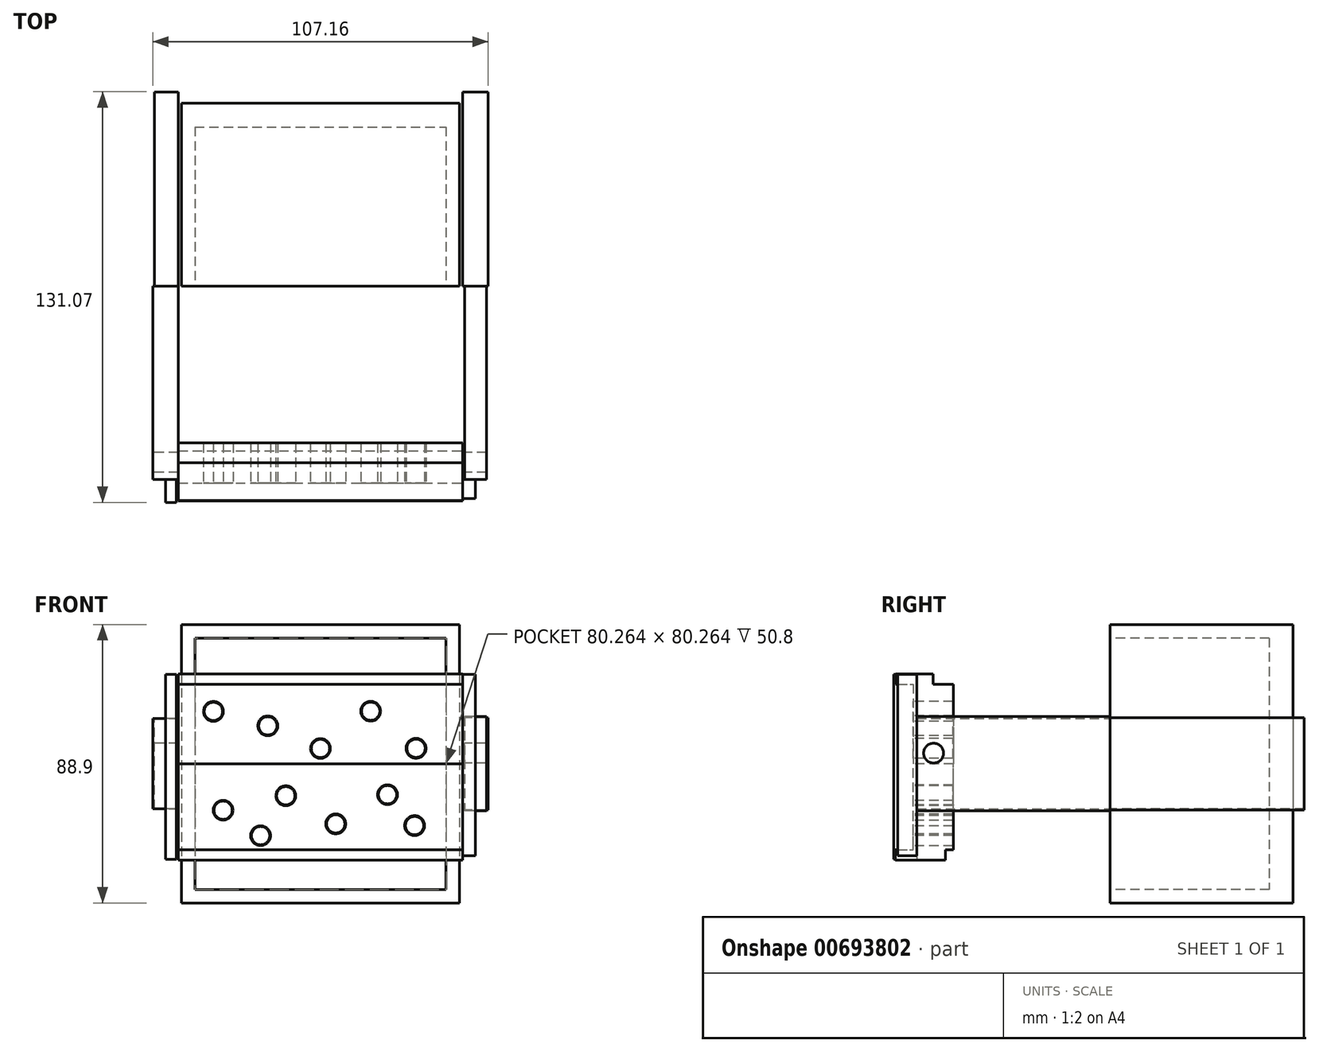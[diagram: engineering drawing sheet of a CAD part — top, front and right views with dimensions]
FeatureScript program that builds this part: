
annotation { "Feature Type Name" : "Feature", "Feature Type Description" : "" }
export const myFeature = defineFeature(function(context is Context, id is Id, definition is map)
    precondition{}
    {
        {
            var Q0;
            Q0=qCreatedBy(makeId("Front.planeOp"),FACE);
            var sketch = newSketch(context, id + "F0", { "sketchPlane" : qUnion([Q0])});
            skLineSegment(sketch, "E0.bottom", {"start": v(-44.45, 44.45) * mm, "end": v(44.45, 44.45) * mm});
            skLineSegment(sketch, "E0.top", {"start": v(-44.45, -44.45) * mm, "end": v(44.45, -44.45) * mm});
            skLineSegment(sketch, "E0.left", {"start": v(-44.45, 44.45) * mm, "end": v(-44.45, -44.45) * mm});
            skLineSegment(sketch, "E0.right", {"start": v(44.45, 44.45) * mm, "end": v(44.45, -44.45) * mm});
            skPoint(sketch, "E0.middle", {"position": v(0, 0) * mm});
            skSolve(sketch);
        }
        {
            var Q0;
            Q0 = qSketchRegion(id + "F0", true);
            extrude(context, id + "F1", {"entities" : qUnion([Q0]), "oppositeDirection" : true, "depth" : 58.42 * mm, "offsetDistance" : 25.4 * mm});
        }
        {
            var Q0;
            Q0=makeQuery(id+"F1.opExtrude","CAP_FACE",FACE,{"disambiguationData":[OSD([sQuery(id+"F0.wireOp",EDGE,"E0.bottom"),sQuery(id+"F0.wireOp",EDGE,"E0.top"),sQuery(id+"F0.wireOp",EDGE,"E0.left"),sQuery(id+"F0.wireOp",EDGE,"E0.right")])],"isStart":true});
            var sketch = newSketch(context, id + "F2", { "sketchPlane" : qUnion([Q0])});
            skLineSegment(sketch, "E1.0", {"start": v(-40.13, 40.13) * mm, "end": v(40.13, 40.13) * mm});
            skLineSegment(sketch, "E1.1", {"start": v(-40.13, 40.13) * mm, "end": v(-40.13, -40.13) * mm});
            skLineSegment(sketch, "E1.2", {"start": v(-40.13, -40.13) * mm, "end": v(40.13, -40.13) * mm});
            skLineSegment(sketch, "E1.3", {"start": v(40.13, 40.13) * mm, "end": v(40.13, -40.13) * mm});
            skSolve(sketch);
        }
        {
            var Q0;
            Q0=makeQuery(id+"F2.imprint","IMPRINT",FACE,{"disambiguationData":[TD([[makeQuery(id+"F2.imprint","IMPRINT",EDGE,{"derivedFrom":sQuery(id+"F2.wireOp",EDGE,"E1.0")}),-1.0]])]});
            extrude(context, id + "F3", {"entities" : qUnion([Q0]), "operationType" : NewBodyOperationType.REMOVE, "oppositeDirection" : true, "depth" : 50.8 * mm, "offsetDistance" : 25.4 * mm});
        }
        {
            var Q0;
            Q0=qCreatedBy(makeId("Front.planeOp"),FACE);
            var sketch = newSketch(context, id + "F4", { "sketchPlane" : qUnion([Q0])});
            skLineSegment(sketch, "E2.bottom", {"start": v(-53, -14.45) * mm, "end": v(-45.4, -14.45) * mm});
            skLineSegment(sketch, "E2.top", {"start": v(-53, 14.45) * mm, "end": v(-45.4, 14.45) * mm});
            skLineSegment(sketch, "E2.left", {"start": v(-53, -14.45) * mm, "end": v(-53, 14.45) * mm});
            skLineSegment(sketch, "E2.right", {"start": v(-45.4, -14.45) * mm, "end": v(-45.4, 14.45) * mm});
            skPoint(sketch, "E2.middle", {"position": v(-49.2, 0) * mm});
            skLineSegment(sketch, "E3.bottom", {"start": v(53.58, 14.75) * mm, "end": v(45.4, 14.75) * mm});
            skLineSegment(sketch, "E3.top", {"start": v(53.58, -14.75) * mm, "end": v(45.4, -14.75) * mm});
            skLineSegment(sketch, "E3.left", {"start": v(53.58, 14.75) * mm, "end": v(53.58, -14.75) * mm});
            skLineSegment(sketch, "E3.right", {"start": v(45.4, 14.75) * mm, "end": v(45.4, -14.75) * mm});
            skPoint(sketch, "E3.middle", {"position": v(49.5, 0) * mm});
            skSolve(sketch);
        }
        {
            var Q0;
            Q0 = qSketchRegion(id + "F4", true);
            extrude(context, id + "F5", {"entities" : qUnion([Q0]), "oppositeDirection" : true, "depth" : 61.98 * mm, "offsetDistance" : 25.4 * mm});
        }
        {
            var Q0;
            Q0=qCreatedBy(makeId("Front.planeOp"),FACE);
            var sketch = newSketch(context, id + "F6", { "sketchPlane" : qUnion([Q0])});
            skLineSegment(sketch, "E4.bottom", {"start": v(-45.4, 14.45) * mm, "end": v(-53.58, 14.45) * mm});
            skLineSegment(sketch, "E4.top", {"start": v(-45.4, -14.45) * mm, "end": v(-53.58, -14.45) * mm});
            skLineSegment(sketch, "E4.left", {"start": v(-45.4, 14.45) * mm, "end": v(-45.4, -14.45) * mm});
            skLineSegment(sketch, "E4.right", {"start": v(-53.58, 14.45) * mm, "end": v(-53.58, -14.45) * mm});
            skPoint(sketch, "E4.middle", {"position": v(-49.5, 0) * mm});
            skLineSegment(sketch, "E5.bottom", {"start": v(53, 15.04) * mm, "end": v(46, 15.04) * mm});
            skLineSegment(sketch, "E5.top", {"start": v(53, -15.04) * mm, "end": v(46, -15.04) * mm});
            skLineSegment(sketch, "E5.left", {"start": v(53, 15.04) * mm, "end": v(53, -15.04) * mm});
            skLineSegment(sketch, "E5.right", {"start": v(46, 15.04) * mm, "end": v(46, -15.04) * mm});
            skPoint(sketch, "E5.middle", {"position": v(49.5, 0) * mm});
            skSolve(sketch);
        }
        {
            var Q0;
            Q0 = qSketchRegion(id + "F6", true);
            extrude(context, id + "F7", {"entities" : qUnion([Q0]), "depth" : 61.72 * mm, "offsetDistance" : 25.4 * mm});
        }
        {
            var Q0;
            Q0=qCreatedBy(makeId("Front.planeOp"),FACE);
            var sketch = newSketch(context, id + "F8", { "sketchPlane" : qUnion([Q0])});
            skLineSegment(sketch, "E6.bottom", {"start": v(-52.7, -14.16) * mm, "end": v(52.7, -14.16) * mm});
            skLineSegment(sketch, "E6.top", {"start": v(-52.7, 14.16) * mm, "end": v(52.7, 14.16) * mm});
            skLineSegment(sketch, "E6.left", {"start": v(-52.7, -14.16) * mm, "end": v(-52.7, 14.16) * mm});
            skLineSegment(sketch, "E6.right", {"start": v(52.7, -14.16) * mm, "end": v(52.7, 14.16) * mm});
            skPoint(sketch, "E6.middle", {"position": v(0, 0) * mm});
            skSolve(sketch);
        }
        {
            var Q0;
            Q0=makeQuery(id+"F8.imprint","IMPRINT",FACE,{"disambiguationData":[TD([[makeQuery(id+"F8.imprint","IMPRINT",EDGE,{"derivedFrom":sQuery(id+"F8.wireOp",EDGE,"E6.bottom")}),1.0]])]});
            extrude(context, id + "F9", {"entities" : qUnion([Q0]), "depth" : 39.12 * mm, "offsetDistance" : 25.4 * mm});
        }
        {
            var Q0;
            Q0=makeQuery(id+"F7.opExtrude","SWEPT_FACE",FACE,{"disambiguationData":[OSD([sQuery(id+"F6.wireOp",EDGE,"E4.right")])]});
            var sketch = newSketch(context, id + "F10", { "sketchPlane" : qUnion([Q0])});
            skLineSegment(sketch, "E7.bottom", {"start": v(51.15, -3.82) * mm, "end": v(61.6, -3.82) * mm});
            skLineSegment(sketch, "E7.top", {"start": v(51.15, 10.58) * mm, "end": v(61.6, 10.58) * mm});
            skLineSegment(sketch, "E7.left", {"start": v(51.15, -3.82) * mm, "end": v(51.15, 10.58) * mm});
            skLineSegment(sketch, "E7.right", {"start": v(61.6, -3.82) * mm, "end": v(61.6, 10.58) * mm});
            skPoint(sketch, "E7.middle", {"position": v(56.38, 3.38) * mm});
            skSolve(sketch);
        }
        {
            var Q0;
            Q0=sQuery(id+"F10.wireOp",VERTEX,"E7.middle");
            var Q1;
            Q1=makeQuery(id+"F7.opExtrude","SWEPT_BODY",BODY,{"disambiguationData":[OSD([sQuery(id+"F6.wireOp",EDGE,"E4.bottom"),sQuery(id+"F6.wireOp",EDGE,"E4.top"),sQuery(id+"F6.wireOp",EDGE,"E4.left"),sQuery(id+"F6.wireOp",EDGE,"E4.right")])]});
            var Q2;
            Q2=makeQuery(id+"F7.opExtrude","SWEPT_BODY",BODY,{"disambiguationData":[OSD([sQuery(id+"F6.wireOp",EDGE,"E5.bottom"),sQuery(id+"F6.wireOp",EDGE,"E5.top"),sQuery(id+"F6.wireOp",EDGE,"E5.left"),sQuery(id+"F6.wireOp",EDGE,"E5.right")])]});
            hole(context, id + "F11", {"style" : HoleStyle.SIMPLE, "endStyle" : HoleEndStyle.THROUGH, "holeDiameter" : 6.35 * mm, "majorDiameter" : 6.35 * mm, "isTappedThrough" : true, "tappedDepth" : 12.7 * mm, "tapClearance" : 3, "locations" : qUnion([Q0]), "scope" : qUnion([Q1, Q2])});
        }
        {
            var Q0;
            Q0=makeQuery(id+"F9.opExtrude","CAP_FACE",FACE,{"disambiguationData":[OSD([sQuery(id+"F8.wireOp",EDGE,"E6.bottom"),sQuery(id+"F8.wireOp",EDGE,"E6.top"),sQuery(id+"F8.wireOp",EDGE,"E6.left"),sQuery(id+"F8.wireOp",EDGE,"E6.right")])],"isStart":false});
            var sketch = newSketch(context, id + "F12", { "sketchPlane" : qUnion([Q0])});
            skLineSegment(sketch, "E8.0", {"start": v(45.34, 6.8) * mm, "end": v(-45.34, 6.8) * mm});
            skLineSegment(sketch, "E8.1", {"start": v(45.34, -6.8) * mm, "end": v(45.34, 6.8) * mm});
            skLineSegment(sketch, "E8.2", {"start": v(-45.34, -6.8) * mm, "end": v(45.34, -6.8) * mm});
            skLineSegment(sketch, "E8.3", {"start": v(-45.34, 6.8) * mm, "end": v(-45.34, -6.8) * mm});
            skSolve(sketch);
        }
        {
            var Q0;
            Q0=makeQuery(id+"F12.imprint","IMPRINT",FACE,{"disambiguationData":[TD([[makeQuery(id+"F12.imprint","IMPRINT",EDGE,{"derivedFrom":sQuery(id+"F12.wireOp",EDGE,"E8.0")}),1.0]])]});
            extrude(context, id + "F13", {"entities" : qUnion([Q0]), "operationType" : NewBodyOperationType.REMOVE, "oppositeDirection" : true, "depth" : 37.85 * mm, "offsetDistance" : 25.4 * mm});
        }
        {
            var Q0;
            Q0=makeQuery(id+"F13.boolean.opBoolean","COPY",FACE,{"derivedFrom":makeQuery(id+"F13.opExtrude","CAP_FACE",FACE,{"disambiguationData":[OSD([sQuery(id+"F12.wireOp",EDGE,"E8.0"),sQuery(id+"F12.wireOp",EDGE,"E8.1"),sQuery(id+"F12.wireOp",EDGE,"E8.2"),sQuery(id+"F12.wireOp",EDGE,"E8.3")])],"isStart":false})});
            var sketch = newSketch(context, id + "F14", { "sketchPlane" : qUnion([Q0])});
            skCircle(sketch, "E9", {"center": v(33.92, 0) * mm, "radius": 2.7 * mm});
            skCircle(sketch, "E10", {"center": v(21.89, 0) * mm, "radius": 2.43 * mm});
            skCircle(sketch, "E11", {"center": v(11.51, 0) * mm, "radius": 2.06 * mm});
            skCircle(sketch, "E12", {"center": v(-12.05, 0) * mm, "radius": 2.2 * mm});
            skCircle(sketch, "E13", {"center": v(-22.16, 0) * mm, "radius": 3.08 * mm});
            skCircle(sketch, "E14", {"center": v(-35.36, 0) * mm, "radius": 3.06 * mm});
            skSolve(sketch);
        }
        {
            var Q0;
            Q0=makeQuery(id+"F14.imprint","IMPRINT",FACE,{"disambiguationData":[TD([[makeQuery(id+"F14.imprint","IMPRINT",EDGE,{"derivedFrom":sQuery(id+"F14.wireOp",EDGE,"E9")}),-1.0]])]});
            extrude(context, id + "F15", {"entities" : qUnion([Q0]), "operationType" : NewBodyOperationType.ADD, "depth" : 25.4 * mm, "offsetDistance" : 25.4 * mm});
        }
        {
            var Q0;
            Q0=makeQuery(id+"F9.opExtrude","SWEPT_BODY",BODY,{"disambiguationData":[OSD([sQuery(id+"F8.wireOp",EDGE,"E6.bottom"),sQuery(id+"F8.wireOp",EDGE,"E6.top"),sQuery(id+"F8.wireOp",EDGE,"E6.left"),sQuery(id+"F8.wireOp",EDGE,"E6.right")])]});
            deleteBodies(context, id + "F16", {"entities" : qUnion([Q0])});
        }
        {
            var Q0;
            Q0=qCreatedBy(makeId("Top.planeOp"),FACE);
            var sketch = newSketch(context, id + "F17", { "sketchPlane" : qUnion([Q0])});
            skLineSegment(sketch, "E15.bottom", {"start": v(-45.4, -50.08) * mm, "end": v(45.4, -50.08) * mm});
            skLineSegment(sketch, "E15.top", {"start": v(-45.4, -62.93) * mm, "end": v(45.4, -62.93) * mm});
            skLineSegment(sketch, "E15.left", {"start": v(-45.4, -50.08) * mm, "end": v(-45.4, -62.93) * mm});
            skLineSegment(sketch, "E15.right", {"start": v(45.4, -50.08) * mm, "end": v(45.4, -62.93) * mm});
            skPoint(sketch, "E15.middle", {"position": v(0, -56.5) * mm});
            skSolve(sketch);
        }
        {
            var Q0;
            Q0 = qSketchRegion(id + "F17", true);
            extrude(context, id + "F18", {"entities" : qUnion([Q0]), "depth" : 25.4 * mm, "offsetDistance" : 25.4 * mm});
        }
        {
            var Q0;
            Q0=makeQuery(id+"F18.opExtrude","CAP_FACE",FACE,{"disambiguationData":[OSD([sQuery(id+"F17.wireOp",EDGE,"E15.bottom"),sQuery(id+"F17.wireOp",EDGE,"E15.top"),sQuery(id+"F17.wireOp",EDGE,"E15.left"),sQuery(id+"F17.wireOp",EDGE,"E15.right")])],"isStart":true});
            var sketch = newSketch(context, id + "F19", { "sketchPlane" : qUnion([Q0])});
            skLineSegment(sketch, "E16.bottom", {"start": v(45.4, 50.08) * mm, "end": v(-45.4, 50.08) * mm});
            skLineSegment(sketch, "E16.top", {"start": v(45.4, 62.93) * mm, "end": v(-45.4, 62.93) * mm});
            skLineSegment(sketch, "E16.left", {"start": v(45.4, 50.08) * mm, "end": v(45.4, 62.93) * mm});
            skLineSegment(sketch, "E16.right", {"start": v(-45.4, 50.08) * mm, "end": v(-45.4, 62.93) * mm});
            skPoint(sketch, "E16.middle", {"position": v(0, 56.5) * mm});
            skPoint(sketch, "E16.middle.positionSnap0", {"position": v(0, 50.08) * mm});
            skPoint(sketch, "E16.centerSnap0", {"position": v(0, 50.08) * mm});
            skSolve(sketch);
        }
        {
            var Q0;
            Q0=makeQuery(id+"F19.imprint","IMPRINT",FACE,{"disambiguationData":[TD([[makeQuery(id+"F19.imprint","IMPRINT",EDGE,{"derivedFrom":sQuery(id+"F19.wireOp",EDGE,"E16.bottom")}),1.0]])]});
            extrude(context, id + "F20", {"entities" : qUnion([Q0]), "depth" : 27.43 * mm, "offsetDistance" : 25.4 * mm});
        }
        {
            var Q0;
            Q0=makeQuery(id+"F20.opExtrude","SWEPT_FACE",FACE,{"disambiguationData":[OSD([sQuery(id+"F19.wireOp",EDGE,"E16.top")])]});
            var sketch = newSketch(context, id + "F21", { "sketchPlane" : qUnion([Q0])});
            skCircle(sketch, "E17", {"center": v(-31.1, -14.85) * mm, "radius": 2.86 * mm});
            skCircle(sketch, "E18", {"center": v(-11.06, -10.24) * mm, "radius": 2.75 * mm});
            skCircle(sketch, "E19", {"center": v(4.87, -19.22) * mm, "radius": 3.28 * mm});
            skCircle(sketch, "E20", {"center": v(21.43, -9.9) * mm, "radius": 3.05 * mm});
            skCircle(sketch, "E21", {"center": v(30.06, -19.77) * mm, "radius": 3.4 * mm});
            skCircle(sketch, "E22", {"center": v(-19.14, -22.98) * mm, "radius": 3.05 * mm});
            skSolve(sketch);
        }
        {
            var Q0;
            Q0=sQuery(id+"F21.wireOp",VERTEX,"E21.center");
            var Q1;
            Q1=sQuery(id+"F21.wireOp",VERTEX,"E20.center");
            var Q2;
            Q2=sQuery(id+"F21.wireOp",VERTEX,"E19.center");
            var Q3;
            Q3=sQuery(id+"F21.wireOp",VERTEX,"E18.center");
            var Q4;
            Q4=sQuery(id+"F21.wireOp",VERTEX,"E22.center");
            var Q5;
            Q5=sQuery(id+"F21.wireOp",VERTEX,"E17.center");
            var Q6;
            Q6=makeQuery(id+"F1.opExtrude","SWEPT_BODY",BODY,{"disambiguationData":[OSD([sQuery(id+"F0.wireOp",EDGE,"E0.bottom"),sQuery(id+"F0.wireOp",EDGE,"E0.top"),sQuery(id+"F0.wireOp",EDGE,"E0.left"),sQuery(id+"F0.wireOp",EDGE,"E0.right")])]});
            var Q7;
            Q7=makeQuery(id+"F20.opExtrude","SWEPT_BODY",BODY,{"disambiguationData":[OSD([sQuery(id+"F19.wireOp",EDGE,"E16.bottom"),sQuery(id+"F19.wireOp",EDGE,"E16.top"),sQuery(id+"F19.wireOp",EDGE,"E16.left"),sQuery(id+"F19.wireOp",EDGE,"E16.right")])]});
            hole(context, id + "F22", {"style" : HoleStyle.SIMPLE, "endStyle" : HoleEndStyle.BLIND, "holeDiameter" : 6.35 * mm, "majorDiameter" : 6.35 * mm, "holeDepth" : 12.7 * mm, "isTappedThrough" : true, "tappedDepth" : 12.7 * mm, "tapClearance" : 3, "locations" : qUnion([Q0, Q1, Q2, Q3, Q4, Q5]), "scope" : qUnion([Q6, Q7])});
        }
        {
            var Q0;
            Q0=makeQuery(id+"F18.opExtrude","SWEPT_FACE",FACE,{"disambiguationData":[OSD([sQuery(id+"F17.wireOp",EDGE,"E15.top")])]});
            var sketch = newSketch(context, id + "F23", { "sketchPlane" : qUnion([Q0])});
            skCircle(sketch, "E23", {"center": v(30.5, 4.92) * mm, "radius": 3.68 * mm});
            skCircle(sketch, "E24", {"center": v(16.02, 16.77) * mm, "radius": 3.52 * mm});
            skCircle(sketch, "E25", {"center": v(0, 4.85) * mm, "radius": 3.45 * mm});
            skCircle(sketch, "E26", {"center": v(-16.82, 12.08) * mm, "radius": 3.3 * mm});
            skCircle(sketch, "E27", {"center": v(-34.18, 16.7) * mm, "radius": 3.81 * mm});
            skSolve(sketch);
        }
        {
            var Q0;
            Q0=sQuery(id+"F23.wireOp",VERTEX,"E23.center");
            var Q1;
            Q1=sQuery(id+"F23.wireOp",VERTEX,"E24.center");
            var Q2;
            Q2=sQuery(id+"F23.wireOp",VERTEX,"E25.center");
            var Q3;
            Q3=sQuery(id+"F23.wireOp",VERTEX,"E26.center");
            var Q4;
            Q4=sQuery(id+"F23.wireOp",VERTEX,"E27.center");
            var Q5;
            Q5=makeQuery(id+"F18.opExtrude","SWEPT_BODY",BODY,{"disambiguationData":[OSD([sQuery(id+"F17.wireOp",EDGE,"E15.bottom"),sQuery(id+"F17.wireOp",EDGE,"E15.top"),sQuery(id+"F17.wireOp",EDGE,"E15.left"),sQuery(id+"F17.wireOp",EDGE,"E15.right")])]});
            hole(context, id + "F24", {"style" : HoleStyle.SIMPLE, "endStyle" : HoleEndStyle.BLIND, "holeDiameter" : 6.35 * mm, "majorDiameter" : 6.35 * mm, "holeDepth" : 12.7 * mm, "isTappedThrough" : true, "tappedDepth" : 12.7 * mm, "tapClearance" : 3, "locations" : qUnion([Q0, Q1, Q2, Q3, Q4]), "scope" : qUnion([Q5])});
        }
        {
            var Q0;
            Q0=makeQuery(id+"F20.opExtrude","CAP_FACE",FACE,{"disambiguationData":[OSD([sQuery(id+"F19.wireOp",EDGE,"E16.bottom"),sQuery(id+"F19.wireOp",EDGE,"E16.top"),sQuery(id+"F19.wireOp",EDGE,"E16.left"),sQuery(id+"F19.wireOp",EDGE,"E16.right")])],"isStart":false});
            var sketch = newSketch(context, id + "F25", { "sketchPlane" : qUnion([Q0])});
            skLineSegment(sketch, "E28.bottom", {"start": v(-45.4, 68.61) * mm, "end": v(45.4, 68.61) * mm});
            skLineSegment(sketch, "E28.top", {"start": v(-45.4, 52.63) * mm, "end": v(45.4, 52.63) * mm});
            skLineSegment(sketch, "E28.left", {"start": v(-45.4, 68.61) * mm, "end": v(-45.4, 52.63) * mm});
            skLineSegment(sketch, "E28.right", {"start": v(45.4, 68.61) * mm, "end": v(45.4, 52.63) * mm});
            skPoint(sketch, "E28.middle", {"position": v(0, 60.62) * mm});
            skSolve(sketch);
        }
        {
            var Q0;
            Q0 = qSketchRegion(id + "F25", true);
            extrude(context, id + "F26", {"entities" : qUnion([Q0]), "operationType" : NewBodyOperationType.ADD, "depth" : 3.3 * mm, "offsetDistance" : 25.4 * mm});
        }
        {
            var Q0;
            Q0=makeQuery(id+"F18.opExtrude","CAP_FACE",FACE,{"disambiguationData":[OSD([sQuery(id+"F17.wireOp",EDGE,"E15.bottom"),sQuery(id+"F17.wireOp",EDGE,"E15.top"),sQuery(id+"F17.wireOp",EDGE,"E15.left"),sQuery(id+"F17.wireOp",EDGE,"E15.right")])],"isStart":false});
            var sketch = newSketch(context, id + "F27", { "sketchPlane" : qUnion([Q0])});
            skLineSegment(sketch, "E29.bottom", {"start": v(45.4, -68.48) * mm, "end": v(-45.4, -68.48) * mm});
            skLineSegment(sketch, "E29.top", {"start": v(45.4, -56.5) * mm, "end": v(-45.4, -56.5) * mm});
            skLineSegment(sketch, "E29.left", {"start": v(45.4, -68.48) * mm, "end": v(45.4, -56.5) * mm});
            skLineSegment(sketch, "E29.right", {"start": v(-45.4, -68.48) * mm, "end": v(-45.4, -56.5) * mm});
            skSolve(sketch);
        }
        {
            var Q0;
            Q0 = qSketchRegion(id + "F27", true);
            extrude(context, id + "F28", {"entities" : qUnion([Q0]), "operationType" : NewBodyOperationType.ADD, "depth" : 3.3 * mm, "offsetDistance" : 25.4 * mm});
        }
        {
            var Q0;
            Q0=makeQuery(id+"F7.opExtrude","CAP_FACE",FACE,{"disambiguationData":[OSD([sQuery(id+"F6.wireOp",EDGE,"E4.bottom"),sQuery(id+"F6.wireOp",EDGE,"E4.top"),sQuery(id+"F6.wireOp",EDGE,"E4.left"),sQuery(id+"F6.wireOp",EDGE,"E4.right")])],"isStart":false});
            var sketch = newSketch(context, id + "F29", { "sketchPlane" : qUnion([Q0])});
            skPoint(sketch, "E30.oppositeSnap0", {"position": v(-49.5, 14.45) * mm});
            skLineSegment(sketch, "E30.bottom", {"start": v(-46, 28.47) * mm, "end": v(-49.5, 28.47) * mm});
            skLineSegment(sketch, "E30.top", {"start": v(-46, -30.51) * mm, "end": v(-49.5, -30.51) * mm});
            skLineSegment(sketch, "E30.left", {"start": v(-46, 28.47) * mm, "end": v(-46, -30.51) * mm});
            skLineSegment(sketch, "E30.right", {"start": v(-49.5, 28.47) * mm, "end": v(-49.5, -30.51) * mm});
            skSolve(sketch);
        }
        {
            var Q0;
            Q0 = qSketchRegion(id + "F29", true);
            extrude(context, id + "F30", {"entities" : qUnion([Q0]), "operationType" : NewBodyOperationType.ADD, "depth" : 7.37 * mm, "offsetDistance" : 25.4 * mm});
        }
        {
            var Q0;
            Q0=makeQuery(id+"F7.opExtrude","CAP_FACE",FACE,{"disambiguationData":[OSD([sQuery(id+"F6.wireOp",EDGE,"E5.bottom"),sQuery(id+"F6.wireOp",EDGE,"E5.top"),sQuery(id+"F6.wireOp",EDGE,"E5.left"),sQuery(id+"F6.wireOp",EDGE,"E5.right")])],"isStart":false});
            var sketch = newSketch(context, id + "F31", { "sketchPlane" : qUnion([Q0])});
            skPoint(sketch, "E31.oppositeSnap0", {"position": v(49.5, -15.04) * mm});
            skLineSegment(sketch, "E31.bottom", {"start": v(45.4, 28.47) * mm, "end": v(49.5, 28.47) * mm});
            skLineSegment(sketch, "E31.top", {"start": v(45.4, -29.35) * mm, "end": v(49.5, -29.35) * mm});
            skLineSegment(sketch, "E31.left", {"start": v(45.4, 28.47) * mm, "end": v(45.4, -29.35) * mm});
            skLineSegment(sketch, "E31.right", {"start": v(49.5, 28.47) * mm, "end": v(49.5, -29.35) * mm});
            skSolve(sketch);
        }
        {
            var Q0;
            Q0 = qSketchRegion(id + "F31", true);
            extrude(context, id + "F32", {"entities" : qUnion([Q0]), "depth" : 6.1 * mm, "offsetDistance" : 25.4 * mm});
        }
    });
